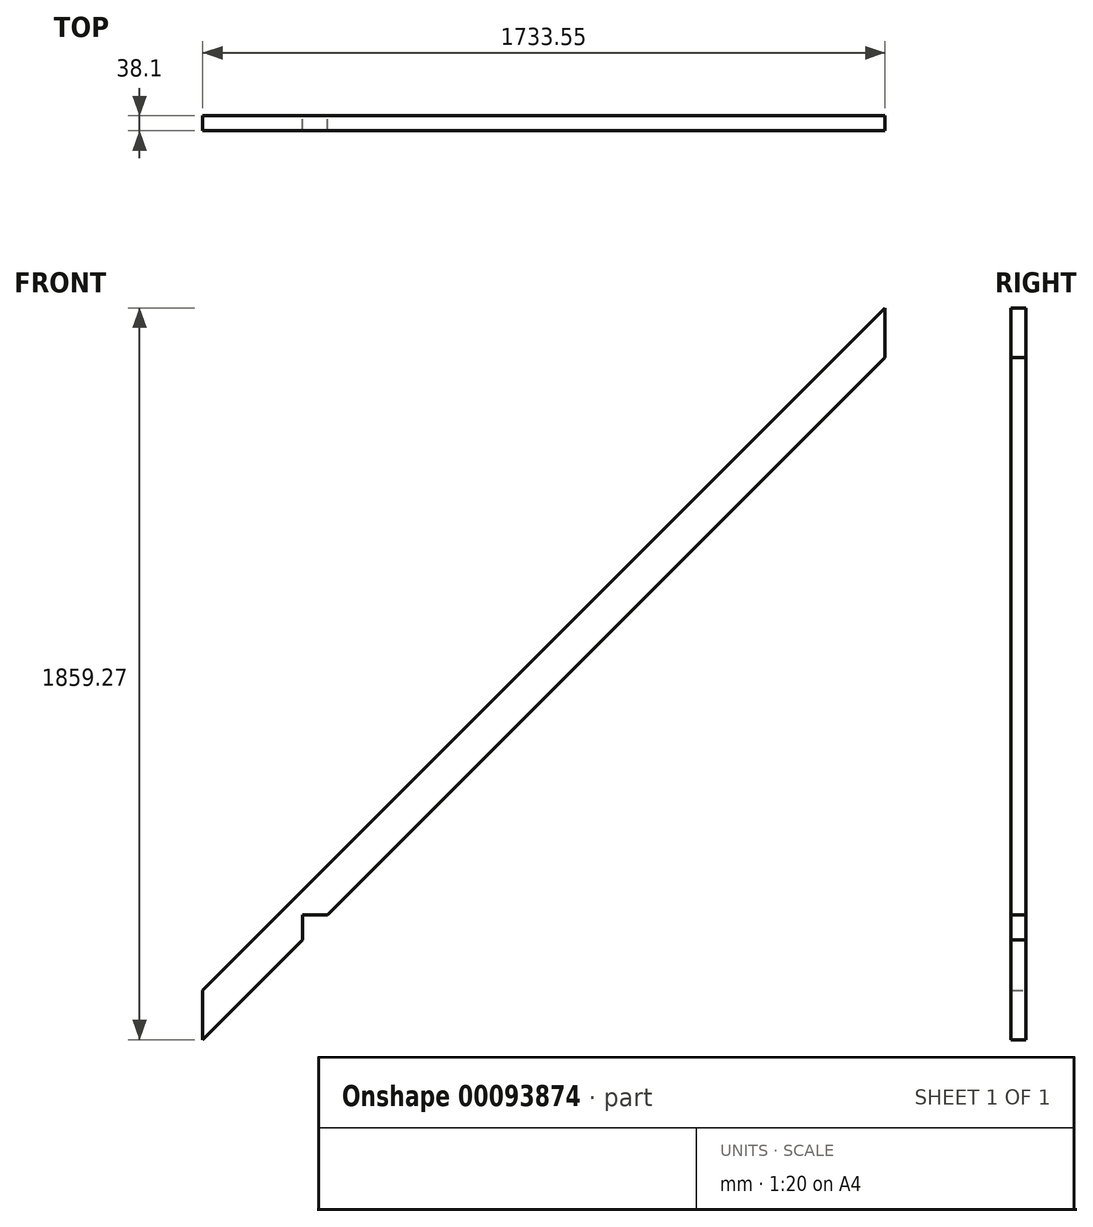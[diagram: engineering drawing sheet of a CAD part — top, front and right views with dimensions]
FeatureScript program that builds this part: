
annotation { "Feature Type Name" : "Feature", "Feature Type Description" : "" }
export const myFeature = defineFeature(function(context is Context, id is Id, definition is map)
    precondition{}
    {
        {
            var Q0;
            Q0=qCreatedBy(makeId("Front.planeOp"),FACE);
            var sketch = newSketch(context, id + "F0", { "sketchPlane" : qUnion([Q0])});
            skLineSegment(sketch, "E0.bottom", {"start": v(-1524, 0) * mm, "end": v(-1435.1, 0) * mm, "construction": true});
            skLineSegment(sketch, "E0.top", {"start": v(-1524, 2120.9) * mm, "end": v(-1435.1, 2120.9) * mm, "construction": true});
            skLineSegment(sketch, "E0.left", {"start": v(-1524, 0) * mm, "end": v(-1524, 2120.9) * mm, "construction": true});
            skLineSegment(sketch, "E0.right", {"start": v(1524, 0) * mm, "end": v(1524, 2120.9) * mm, "construction": true});
            skLineSegment(sketch, "E1", {"start": v(-1524, 2120.9) * mm, "end": v(0, 3644.9) * mm, "construction": true});
            skLineSegment(sketch, "E2", {"start": v(-1435.1, 2120.9) * mm, "end": v(-1435.1, 101.6) * mm, "construction": true});
            skLineSegment(sketch, "E3", {"start": v(-1435.1, 101.6) * mm, "end": v(-812.8, 101.6) * mm, "construction": true});
            skLineSegment(sketch, "E4", {"start": v(1422.4, 2120.9) * mm, "end": v(1422.4, 101.6) * mm, "construction": true});
            skLineSegment(sketch, "E5.trimOffspring", {"start": v(1422.4, 2120.9) * mm, "end": v(1524, 2120.9) * mm, "construction": true});
            skLineSegment(sketch, "E6", {"start": v(-1435.1, 101.6) * mm, "end": v(-1435.1, 0) * mm, "construction": true});
            skLineSegment(sketch, "E7", {"start": v(1422.4, 101.6) * mm, "end": v(1422.4, 0) * mm, "construction": true});
            skLineSegment(sketch, "E8", {"start": v(-1435.1, 0) * mm, "end": v(1422.4, 0) * mm, "construction": true});
            skLineSegment(sketch, "E9", {"start": v(1422.4, 0) * mm, "end": v(1524, 0) * mm, "construction": true});
            skLineSegment(sketch, "E10", {"start": v(0, 3644.9) * mm, "end": v(0, 0) * mm, "construction": true});
            skLineSegment(sketch, "E11", {"start": v(-762, 2882.9) * mm, "end": v(-762, 0) * mm, "construction": true});
            skLineSegment(sketch, "E12", {"start": v(764.92, 2873.77) * mm, "end": v(764.92, 0) * mm, "construction": true});
            skLineSegment(sketch, "E13", {"start": v(-812.8, 101.6) * mm, "end": v(-711.2, 101.6) * mm, "construction": true});
            skLineSegment(sketch, "E14", {"start": v(-711.2, 101.6) * mm, "end": v(-50.8, 101.6) * mm, "construction": true});
            skLineSegment(sketch, "E15", {"start": v(-50.8, 101.6) * mm, "end": v(50.8, 101.6) * mm, "construction": true});
            skLineSegment(sketch, "E16", {"start": v(50.8, 101.6) * mm, "end": v(711.2, 101.6) * mm, "construction": true});
            skLineSegment(sketch, "E17", {"start": v(711.2, 101.6) * mm, "end": v(812.8, 101.6) * mm, "construction": true});
            skLineSegment(sketch, "E18", {"start": v(812.8, 101.6) * mm, "end": v(1422.4, 101.6) * mm, "construction": true});
            skLineSegment(sketch, "E19", {"start": v(0, 3644.9) * mm, "end": v(1524, 2120.9) * mm, "construction": true});
            skLineSegment(sketch, "E20", {"start": v(-1467.17, 2114.87) * mm, "end": v(-705.17, 2876.87) * mm, "construction": true});
            skLineSegment(sketch, "E21", {"start": v(0, 3582.04) * mm, "end": v(1473.2, 2120.9) * mm, "construction": true});
            skLineSegment(sketch, "E22", {"start": v(-806.45, 2775.59) * mm, "end": v(-806.45, 101.6) * mm, "construction": true});
            skLineSegment(sketch, "E23", {"start": v(-705.17, 2876.87) * mm, "end": v(0, 3582.04) * mm, "construction": true});
            skLineSegment(sketch, "E24", {"start": v(-44.45, 3537.59) * mm, "end": v(-44.45, 101.6) * mm, "construction": true});
            skLineSegment(sketch, "E25", {"start": v(44.45, 3537.95) * mm, "end": v(44.45, 101.6) * mm, "construction": true});
            skLineSegment(sketch, "E26", {"start": v(714.12, 2873.77) * mm, "end": v(714.12, 101.6) * mm, "construction": true});
            skLineSegment(sketch, "E27", {"start": v(815.72, 2773) * mm, "end": v(815.72, 101.6) * mm, "construction": true});
            skLineSegment(sketch, "E28", {"start": v(-717.55, 2864.49) * mm, "end": v(-717.55, 101.6) * mm, "construction": true});
            skLineSegment(sketch, "E29.bottom", {"start": v(-44.45, 3537.59) * mm, "end": v(44.45, 3537.59) * mm, "construction": true});
            skLineSegment(sketch, "E29.top", {"start": v(-44.45, 3677.29) * mm, "end": v(44.45, 3677.29) * mm, "construction": true});
            skLineSegment(sketch, "E29.left", {"start": v(-44.45, 3537.59) * mm, "end": v(-44.45, 3677.29) * mm, "construction": true});
            skLineSegment(sketch, "E29.right", {"start": v(44.45, 3537.59) * mm, "end": v(44.45, 3677.29) * mm, "construction": true});
            skLineSegment(sketch, "E30", {"start": v(-1524, 2120.9) * mm, "end": v(-1524, 2058.04) * mm});
            skLineSegment(sketch, "E31", {"start": v(-1524, 2058.04) * mm, "end": v(-1778, 1804.04) * mm});
            skLineSegment(sketch, "E32", {"start": v(-1778, 1804.04) * mm, "end": v(-1778, 1929.76) * mm});
            skLineSegment(sketch, "E33", {"start": v(-1778, 1929.76) * mm, "end": v(-44.45, 3663.31) * mm});
            skLineSegment(sketch, "E34", {"start": v(-44.45, 3663.31) * mm, "end": v(-44.45, 3537.59) * mm});
            skLineSegment(sketch, "E35", {"start": v(-1524, 2120.9) * mm, "end": v(-1461.14, 2120.9) * mm});
            skLineSegment(sketch, "E36", {"start": v(-1461.14, 2120.9) * mm, "end": v(-44.45, 3537.59) * mm});
            skLineSegment(sketch, "E37", {"start": v(-1778, 1804.04) * mm, "end": v(-1869.51, 1895.55) * mm, "construction": true});
            skLineSegment(sketch, "E38", {"start": v(-1778, 1929.76) * mm, "end": v(-1840.86, 1866.9) * mm, "construction": true});
            skSolve(sketch);
        }
        {
            var Q0;
            Q0=qSketchRegion(id+"F0",true);
            extrude(context, id + "F1", {"entities" : qUnion([Q0]), "depth" : 38.1 * mm});
        }
    });
